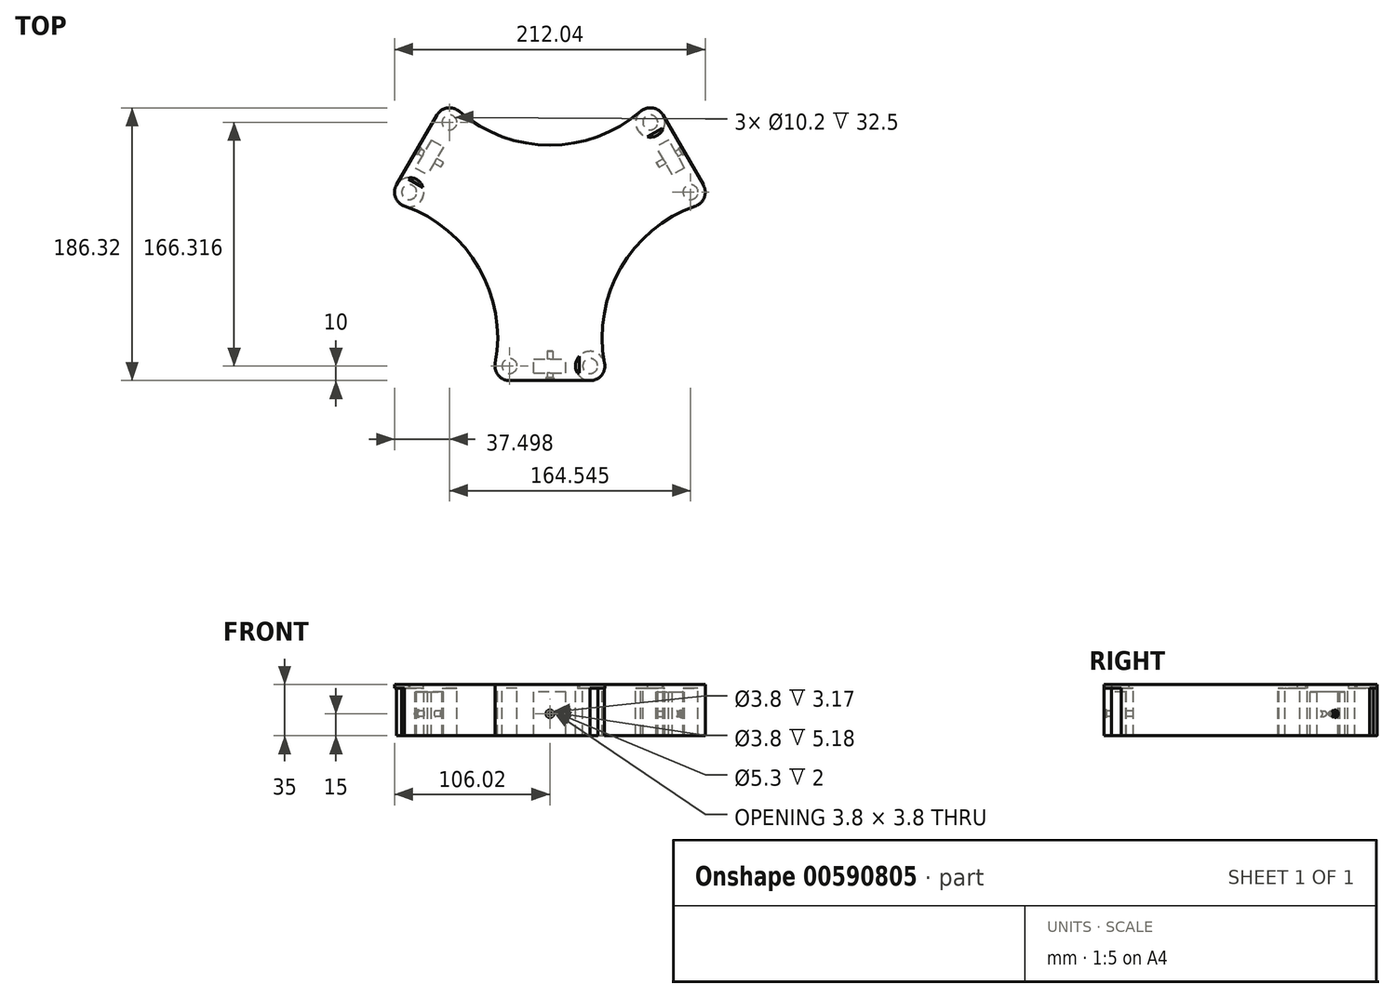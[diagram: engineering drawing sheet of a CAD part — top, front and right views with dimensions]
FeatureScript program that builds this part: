
annotation { "Feature Type Name" : "Feature", "Feature Type Description" : "" }
export const myFeature = defineFeature(function(context is Context, id is Id, definition is map)
    precondition{}
    {
        {
            var Q0;
            Q0=qCreatedBy(makeId("Top.planeOp"),FACE);
            var sketch = newSketch(context, id + "F0", { "sketchPlane" : qUnion([Q0])});
            skCircle(sketch, "E0", {"center": v(0, 0) * mm, "radius": 57.15 * mm, "construction": true});
            skLineSegment(sketch, "E1.bottom", {"start": v(110, 110) * mm, "end": v(-110, 110) * mm, "construction": true});
            skLineSegment(sketch, "E1.top", {"start": v(110, -110) * mm, "end": v(-110, -110) * mm, "construction": true});
            skLineSegment(sketch, "E1.left", {"start": v(110, 110) * mm, "end": v(110, -110) * mm, "construction": true});
            skLineSegment(sketch, "E1.right", {"start": v(-110, 110) * mm, "end": v(-110, -110) * mm, "construction": true});
            skLineSegment(sketch, "E2", {"start": v(0, 0) * mm, "end": v(0, -95) * mm});
            skLineSegment(sketch, "E3", {"start": v(0, 0) * mm, "end": v(-75.93, -43.84) * mm});
            skLineSegment(sketch, "E4", {"start": v(0, 0) * mm, "end": v(-69.24, 39.98) * mm});
            skLineSegment(sketch, "E5.MirrorCS", {"start": v(0, 0) * mm, "end": v(75.93, -43.84) * mm});
            skLineSegment(sketch, "E6.MirrorCS", {"start": v(0, 0) * mm, "end": v(69.24, 39.98) * mm});
            skCircle(sketch, "E7", {"center": v(-27.5, -95) * mm, "radius": 5.1 * mm});
            skCircle(sketch, "E8", {"center": v(-27.5, -95) * mm, "radius": 10 * mm});
            skCircle(sketch, "E9.MirrorC", {"center": v(27.5, -95) * mm, "radius": 10 * mm});
            skCircle(sketch, "E10.MirrorC", {"center": v(27.5, -95) * mm, "radius": 5.1 * mm});
            skLineSegment(sketch, "E11", {"start": v(-27.5, -105) * mm, "end": v(27.5, -105) * mm});
            skCircle(sketch, "E12.1.0", {"center": v(68.52, 71.32) * mm, "radius": 10 * mm});
            skCircle(sketch, "E12.1.1", {"center": v(68.52, 71.32) * mm, "radius": 5.1 * mm});
            skLineSegment(sketch, "E12.1.2", {"start": v(104.68, 28.68) * mm, "end": v(77.18, 76.32) * mm});
            skCircle(sketch, "E12.1.3", {"center": v(96.02, 23.68) * mm, "radius": 10 * mm});
            skCircle(sketch, "E12.1.4", {"center": v(96.02, 23.68) * mm, "radius": 5.1 * mm});
            skCircle(sketch, "E12.2.0", {"center": v(-96.02, 23.68) * mm, "radius": 10 * mm});
            skCircle(sketch, "E12.2.1", {"center": v(-96.02, 23.68) * mm, "radius": 5.1 * mm});
            skLineSegment(sketch, "E12.2.2", {"start": v(-77.18, 76.32) * mm, "end": v(-104.68, 28.68) * mm});
            skCircle(sketch, "E12.2.3", {"center": v(-68.52, 71.32) * mm, "radius": 10 * mm});
            skCircle(sketch, "E12.2.4", {"center": v(-68.52, 71.32) * mm, "radius": 5.1 * mm});
            skArc(sketch, "E13", {"start": v(99.32, 14.24) * mm, "mid": v(48.39, -27.94) * mm, "end": v(37.32, -93.14) * mm});
            skArc(sketch, "E14.1.0", {"start": v(-62, 78.9) * mm, "mid": v(0, 55.87) * mm, "end": v(62, 78.9) * mm});
            skArc(sketch, "E14.2.0", {"start": v(-37.32, -93.14) * mm, "mid": v(-48.39, -27.94) * mm, "end": v(-99.32, 14.24) * mm});
            skSolve(sketch);
        }
        {
            var Q0;
            {var subQ0=sQuery(id+"F0.wireOp",EDGE,"E11");Q0=makeQuery(id+"F0.imprint","IMPRINT",FACE,{"disambiguationData":[TD([[makeQuery(id+"F0.imprint","IMPRINT",EDGE,{"derivedFrom":subQ0}),1.0]])]});}
            var Q1;
            Q1=makeQuery(id+"F0.imprint","IMPRINT",FACE,{"disambiguationData":[TD([[makeQuery(id+"F0.imprint","IMPRINT",EDGE,{"derivedFrom":sQuery(id+"F0.wireOp",EDGE,"E10.MirrorC")}),1.0]])]});
            var Q2;
            Q2=makeQuery(id+"F0.imprint","IMPRINT",FACE,{"disambiguationData":[TD([[makeQuery(id+"F0.imprint","IMPRINT",EDGE,{"derivedFrom":sQuery(id+"F0.wireOp",EDGE,"E7")}),-1.0]])]});
            extrude(context, id + "F1", {"entities" : qUnion([Q0, Q1, Q2]), "oppositeDirection" : true, "depth" : 35 * mm, "offsetDistance" : 25 * mm});
        }
        {
            var Q0;
            Q0=makeQuery(id+"F1.opExtrude","CAP_FACE",FACE,{"disambiguationData":[OSD([sQuery(id+"F0.wireOp",EDGE,"E3"),sQuery(id+"F0.wireOp",EDGE,"E5.MirrorCS"),sQuery(id+"F0.wireOp",EDGE,"E7"),sQuery(id+"F0.wireOp",EDGE,"E8"),sQuery(id+"F0.wireOp",EDGE,"E9.MirrorC"),sQuery(id+"F0.wireOp",EDGE,"E10.MirrorC"),sQuery(id+"F0.wireOp",EDGE,"E11"),sQuery(id+"F0.wireOp",EDGE,"E13"),sQuery(id+"F0.wireOp",EDGE,"E14.2.0")])],"isStart":true});
            var sketch = newSketch(context, id + "F2", { "sketchPlane" : qUnion([Q0])});
            skLineSegment(sketch, "E15.0", {"start": v(-27.5, -105) * mm, "end": v(27.5, -105) * mm});
            skLineSegment(sketch, "E16.bottom", {"start": v(11, -90.18) * mm, "end": v(-11, -90.18) * mm});
            skLineSegment(sketch, "E16.top", {"start": v(11, -99.83) * mm, "end": v(-11, -99.83) * mm});
            skLineSegment(sketch, "E16.left", {"start": v(11, -90.18) * mm, "end": v(11, -99.83) * mm});
            skLineSegment(sketch, "E16.right", {"start": v(-11, -90.18) * mm, "end": v(-11, -99.83) * mm});
            skPoint(sketch, "E16.middle", {"position": v(0, -95) * mm});
            skPoint(sketch, "E16.middle.positionSnap0", {"position": v(0, -105) * mm});
            skPoint(sketch, "E16.centerSnap0", {"position": v(0, -105) * mm});
            skSolve(sketch);
        }
        {
            var Q0;
            Q0=makeQuery(id+"F2.imprint","IMPRINT",FACE,{"disambiguationData":[TD([[makeQuery(id+"F2.imprint","IMPRINT",EDGE,{"derivedFrom":sQuery(id+"F2.wireOp",EDGE,"E16.bottom")}),1.0]])]});
            var Q1;
            Q1=makeQuery(id+"F1.opExtrude","CAP_FACE",FACE,{"disambiguationData":[OSD([sQuery(id+"F0.wireOp",EDGE,"E3"),sQuery(id+"F0.wireOp",EDGE,"E5.MirrorCS"),sQuery(id+"F0.wireOp",EDGE,"E7"),sQuery(id+"F0.wireOp",EDGE,"E8"),sQuery(id+"F0.wireOp",EDGE,"E9.MirrorC"),sQuery(id+"F0.wireOp",EDGE,"E10.MirrorC"),sQuery(id+"F0.wireOp",EDGE,"E11"),sQuery(id+"F0.wireOp",EDGE,"E13"),sQuery(id+"F0.wireOp",EDGE,"E14.2.0")])],"isStart":false});
            extrude(context, id + "F3", {"entities" : qUnion([Q0]), "operationType" : NewBodyOperationType.REMOVE, "endBound" : BoundingType.UP_TO_SURFACE, "oppositeDirection" : true, "depth" : 25 * mm, "endBoundEntityFace" : qUnion([Q1]), "offsetDistance" : 25 * mm});
        }
        {
            var Q0;
            Q0=makeQuery(id+"F2.imprint","IMPRINT",FACE,{"disambiguationData":[TD([[makeQuery(id+"F2.imprint","IMPRINT",EDGE,{"derivedFrom":sQuery(id+"F2.wireOp",EDGE,"E16.bottom")}),1.0]])]});
            extrude(context, id + "F4", {"entities" : qUnion([Q0]), "operationType" : NewBodyOperationType.ADD, "oppositeDirection" : true, "depth" : 5 * mm, "offsetDistance" : 25 * mm});
        }
        {
            var Q0;
            Q0=makeQuery(id+"F0.imprint","IMPRINT",FACE,{"disambiguationData":[TD([[makeQuery(id+"F0.imprint","IMPRINT",EDGE,{"derivedFrom":sQuery(id+"F0.wireOp",EDGE,"E10.MirrorC")}),-1.0]])]});
            var Q1;
            Q1=makeQuery(id+"F0.imprint","IMPRINT",FACE,{"disambiguationData":[TD([[makeQuery(id+"F0.imprint","IMPRINT",EDGE,{"derivedFrom":sQuery(id+"F0.wireOp",EDGE,"E7")}),1.0]])]});
            var Q2;
            Q2=sQuery(id+"F0.wireOp",EDGE,"E10.MirrorC");
            var Q3;
            Q3=sQuery(id+"F0.wireOp",EDGE,"E7");
            extrude(context, id + "F5", {"entities" : qUnion([Q0, Q1]), "operationType" : NewBodyOperationType.ADD, "surfaceEntities" : qUnion([Q2, Q3]), "oppositeDirection" : true, "depth" : 2.5 * mm, "offsetDistance" : 25 * mm});
        }
        {
            var Q0;
            Q0=makeQuery(id+"F1.opExtrude","SWEPT_FACE",FACE,{"disambiguationData":[OSD([sQuery(id+"F0.wireOp",EDGE,"E11")])]});
            var sketch = newSketch(context, id + "F6", { "sketchPlane" : qUnion([Q0])});
            skLineSegment(sketch, "E17.0", {"start": v(-27.5, -35) * mm, "end": v(27.5, -35) * mm});
            skLineSegment(sketch, "E18.0", {"start": v(-27.5, 0) * mm, "end": v(27.5, 0) * mm});
            skLineSegment(sketch, "E19", {"start": v(0, 0) * mm, "end": v(0, -35) * mm, "construction": true});
            skPoint(sketch, "E20", {"position": v(0, -17.5) * mm});
            skCircle(sketch, "E21", {"center": v(0, -20) * mm, "radius": 4.15 * mm});
            skCircle(sketch, "E22", {"center": v(0, -20) * mm, "radius": 2.65 * mm});
            skCircle(sketch, "E23", {"center": v(0, -20) * mm, "radius": 1.9 * mm});
            skSolve(sketch);
        }
        {
            var Q0;
            Q0=makeQuery(id+"F6.imprint","IMPRINT",FACE,{"disambiguationData":[TD([[makeQuery(id+"F6.imprint","IMPRINT",EDGE,{"derivedFrom":sQuery(id+"F6.wireOp",EDGE,"E23")}),1.0]])]});
            extrude(context, id + "F7", {"entities" : qUnion([Q0]), "operationType" : NewBodyOperationType.REMOVE, "oppositeDirection" : true, "depth" : 20 * mm, "offsetDistance" : 25 * mm});
        }
        {
            var Q0;
            Q0=makeQuery(id+"F6.imprint","IMPRINT",FACE,{"disambiguationData":[TD([[makeQuery(id+"F6.imprint","IMPRINT",EDGE,{"derivedFrom":sQuery(id+"F6.wireOp",EDGE,"E22")}),1.0]])]});
            extrude(context, id + "F8", {"entities" : qUnion([Q0]), "operationType" : NewBodyOperationType.REMOVE, "oppositeDirection" : true, "depth" : 2 * mm, "offsetDistance" : 25 * mm});
        }
        {
            var Q0;
            Q0=makeQuery(id+"F1.opExtrude","CAP_FACE",FACE,{"disambiguationData":[OSD([sQuery(id+"F0.wireOp",EDGE,"E3"),sQuery(id+"F0.wireOp",EDGE,"E5.MirrorCS"),sQuery(id+"F0.wireOp",EDGE,"E7"),sQuery(id+"F0.wireOp",EDGE,"E8"),sQuery(id+"F0.wireOp",EDGE,"E9.MirrorC"),sQuery(id+"F0.wireOp",EDGE,"E10.MirrorC"),sQuery(id+"F0.wireOp",EDGE,"E11"),sQuery(id+"F0.wireOp",EDGE,"E13"),sQuery(id+"F0.wireOp",EDGE,"E14.2.0")])],"isStart":false});
            var sketch = newSketch(context, id + "F9", { "sketchPlane" : qUnion([Q0])});
            skLineSegment(sketch, "E24.bottom", {"start": v(20.03, 99.83) * mm, "end": v(13.38, 99.83) * mm});
            skLineSegment(sketch, "E24.top", {"start": v(20.03, 79.43) * mm, "end": v(13.38, 79.43) * mm});
            skLineSegment(sketch, "E24.left", {"start": v(20.03, 99.83) * mm, "end": v(20.03, 79.43) * mm});
            skLineSegment(sketch, "E24.right", {"start": v(13.38, 99.83) * mm, "end": v(13.38, 79.43) * mm});
            skPoint(sketch, "E24.middle", {"position": v(16.7, 89.63) * mm});
            skLineSegment(sketch, "E25", {"start": v(11, 95) * mm, "end": v(13.38, 95) * mm});
            skLineSegment(sketch, "E26", {"start": v(20.03, 95) * mm, "end": v(22.4, 95) * mm});
            skSolve(sketch);
        }
        {
            var Q0;
            {var subQ3=sQuery(id+"F9.wireOp",EDGE,"E24.bottom");Q0=makeQuery(id+"F9.imprint","IMPRINT",FACE,{"disambiguationData":[TD([[makeQuery(id+"F9.imprint","IMPRINT",EDGE,{"derivedFrom":subQ3}),1.0]])]});}
            var Q1;
            {var subQ0=sQuery(id+"F0.wireOp",EDGE,"E10.MirrorC");var subQ1=sQuery(id+"F0.wireOp",EDGE,"E7");Q1=makeQuery(id+"F5.boolean.opBoolean","MERGE",FACE,{"derivedFrom":[makeQuery(id+"F4.boolean.opBoolean","MERGE",FACE,{"derivedFrom":[makeQuery(id+"F1.opExtrude","CAP_FACE",FACE,{"disambiguationData":[OSD([sQuery(id+"F0.wireOp",EDGE,"E3"),sQuery(id+"F0.wireOp",EDGE,"E5.MirrorCS"),subQ1,sQuery(id+"F0.wireOp",EDGE,"E8"),sQuery(id+"F0.wireOp",EDGE,"E9.MirrorC"),subQ0,sQuery(id+"F0.wireOp",EDGE,"E11"),sQuery(id+"F0.wireOp",EDGE,"E13"),sQuery(id+"F0.wireOp",EDGE,"E14.2.0")])],"isStart":true}),makeQuery(id+"F4.opExtrude","CAP_FACE",FACE,{"disambiguationData":[OSD([sQuery(id+"F2.wireOp",EDGE,"E16.bottom"),sQuery(id+"F2.wireOp",EDGE,"E16.top"),sQuery(id+"F2.wireOp",EDGE,"E16.left"),sQuery(id+"F2.wireOp",EDGE,"E16.right")])],"isStart":true})]}),makeQuery(id+"F5.opExtrude","CAP_FACE",FACE,{"disambiguationData":[OSD([subQ1])],"isStart":true}),makeQuery(id+"F5.opExtrude","CAP_FACE",FACE,{"disambiguationData":[OSD([subQ0])],"isStart":true})]});}
            extrude(context, id + "F10", {"entities" : qUnion([Q0]), "operationType" : NewBodyOperationType.REMOVE, "endBound" : BoundingType.UP_TO_SURFACE, "oppositeDirection" : true, "depth" : 25 * mm, "endBoundEntityFace" : qUnion([Q1]), "offsetDistance" : 25 * mm});
        }
        {
            var Q0;
            Q0=makeQuery(id+"F1.opExtrude","SWEPT_BODY",BODY,{"disambiguationData":[OSD([sQuery(id+"F0.wireOp",EDGE,"E3"),sQuery(id+"F0.wireOp",EDGE,"E5.MirrorCS"),sQuery(id+"F0.wireOp",EDGE,"E7"),sQuery(id+"F0.wireOp",EDGE,"E8"),sQuery(id+"F0.wireOp",EDGE,"E9.MirrorC"),sQuery(id+"F0.wireOp",EDGE,"E10.MirrorC"),sQuery(id+"F0.wireOp",EDGE,"E11"),sQuery(id+"F0.wireOp",EDGE,"E13"),sQuery(id+"F0.wireOp",EDGE,"E14.2.0")])]});
            var Q1;
            Q1=sQuery(id+"F0.wireOp",EDGE,"E0");
            circularPattern(context, id + "F11", {"operationType" : NewBodyOperationType.ADD, "entities" : qUnion([Q0]), "axis" : qUnion([Q1]), "angle" : 360 * degree, "instanceCount" : 3, "equalSpace" : true});
        }
    });
